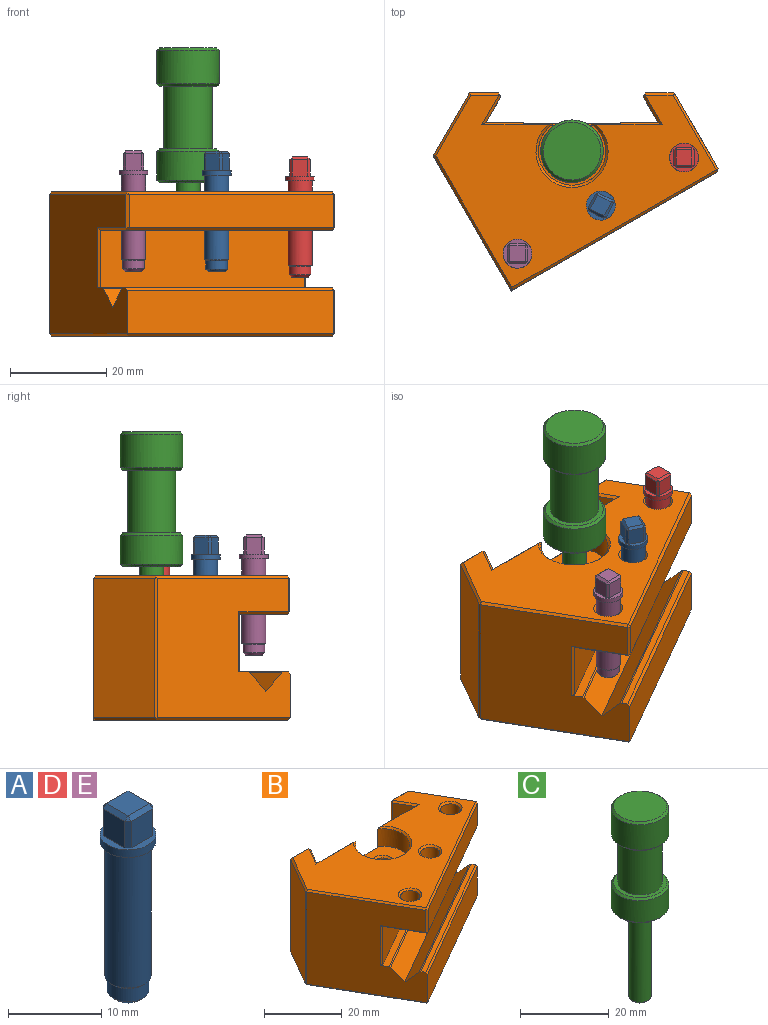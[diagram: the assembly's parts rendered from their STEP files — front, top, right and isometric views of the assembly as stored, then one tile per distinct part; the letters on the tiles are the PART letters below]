
ASSEMBLY  parts=5 mates=4
PART A: 25 faces, bbox 6x6x25 mm
  f0: cylinder r=3mm len=6mm, axis (0,0,-1), area 18.8mm2, adj f3,f5
  f1: cylinder r=2.25mm len=4.5mm, axis (0,0,-1), area 24.7mm2, adj f23,f24
  f2: plane 3.5x3.5mm, normal (0,0,-1), area 9.6mm2, adj f23
  f3: plane 6x6mm, normal (0,0,-1), area 8.6mm2, adj f0,f4
  f4: cylinder r=2.5mm len=17.5mm, axis (0,0,-1), area 274.9mm2, adj f3,f24
  f5: plane 6x6mm, normal (0,0,1), area 10.8mm2, adj f0,f6,f7,f8,f9,f11,f13,f16
  f6: plane 3.5x3.24mm, normal (0,1,0), area 11.3mm2, adj f5,f13,f19,f22
  f7: plane 3.5x3.24mm, normal (1,0,0), area 11.3mm2, adj f5,f11,f13,f14
  f8: plane 3.5x3.24mm, normal (0,-1,0), area 11.3mm2, adj f5,f11,f15,f16
  f9: plane 3.5x3.24mm, normal (-1,0,0), area 11.3mm2, adj f5,f16,f20,f22
  f10: plane 3.24x3.24mm, normal (0,0,1), area 10.5mm2, adj f14,f15,f19,f20
  f11: plane 3.5x0.5mm, normal (0.71,-0.71,0), area 2.5mm2, adj f5,f7,f8,f12
  f12: plane 0.5x0.5mm, normal (0.58,-0.58,0.58), area 0.2mm2, adj f11,f14,f15
  f13: plane 3.5x0.5mm, normal (0.71,0.71,0), area 2.5mm2, adj f5,f6,f7,f17
  f14: plane 3.24x0.5mm, normal (0.71,0,0.71), area 2.3mm2, adj f7,f10,f12,f17
  f15: plane 3.24x0.5mm, normal (0,-0.71,0.71), area 2.3mm2, adj f8,f10,f12,f18
  f16: plane 3.5x0.5mm, normal (-0.71,-0.71,0), area 2.5mm2, adj f5,f8,f9,f18
  f17: plane 0.5x0.5mm, normal (0.58,0.58,0.58), area 0.2mm2, adj f13,f14,f19
  f18: plane 0.5x0.5mm, normal (-0.58,-0.58,0.58), area 0.2mm2, adj f15,f16,f20
  f19: plane 3.24x0.5mm, normal (0,0.71,0.71), area 2.3mm2, adj f6,f10,f17,f21
  f20: plane 3.24x0.5mm, normal (-0.71,0,0.71), area 2.3mm2, adj f9,f10,f18,f21
  f21: plane 0.5x0.5mm, normal (-0.58,0.58,0.58), area 0.2mm2, adj f19,f20,f22
  f22: plane 3.5x0.5mm, normal (-0.71,0.71,0), area 2.5mm2, adj f5,f6,f9,f21
  f23: cone r=1.75mm half-angle=45deg, axis (0,0,1), area 8.9mm2, adj f1,f2
  f24: cone r=2mm half-angle=45deg, axis (0,0,1), area 5.3mm2, adj f1,f4
PART B: 89 faces, bbox 59.1x41.1x30 mm
  f0: plane 29x7.91mm, normal (0,1,0), area 229.4mm2, adj f2,f4,f14,f86
  f1: cylinder r=7mm len=14mm, axis (0,0,1), area 196.3mm2, adj f3,f5,f21,f88
  f2: plane 14.51x0.5mm, normal (0,0.71,0.71), area 8.2mm2, adj f0,f3,f19,f30,f86,f88
  f3: cone r=7mm half-angle=45deg, axis (0,0,1), area 25.4mm2, adj f1,f2,f19,f32,f88
  f4: plane 37.56x0.5mm, normal (0,0.71,-0.71), area 20.3mm2, adj f0,f11,f20,f33,f34,f86,f87,f88
  f5: plane 8.67x0.31mm, normal (0,0.71,0.71), area 3.5mm2, adj f1,f21,f88
  f6: plane 42.44x24.5mm, normal (0.5,-0.87,0), area 343mm2, adj f40,f41,f52,f53
  f7: plane 29x15.44mm, normal (0.87,0.5,0), area 343.4mm2, adj f53,f54,f61,f62,f64,f65,f68,f71
  f8: cylinder r=2.5mm len=7mm, axis (0,0,1), area 110mm2, adj f79,f80
  f9: cylinder r=2.5mm len=7mm, axis (0,0,1), area 110mm2, adj f81,f82
  f10: cylinder r=2.5mm len=7mm, axis (0,0,1), area 110mm2, adj f83,f84
  f11: plane 29x7.91mm, normal (0,1,0), area 229.4mm2, adj f4,f13,f32,f87
  f12: plane 29.5x5.81mm, normal (0,1,0), area 171.3mm2, adj f20,f43,f55,f62,f65
  f13: plane 29x5.4mm, normal (-0.87,-0.5,0), area 180.8mm2, adj f11,f33,f42,f43
  f14: plane 29x5.4mm, normal (0.87,-0.5,0), area 180.8mm2, adj f0,f30,f34,f35
  f15: plane 29x6.12mm, normal (0,1,0), area 177.3mm2, adj f16,f35,f36,f50
  f16: plane 29x12.8mm, normal (-0.87,0.5,0), area 428.6mm2, adj f15,f45,f56,f57
  f17: plane 29x27.83mm, normal (-0.87,-0.5,0), area 755.9mm2, adj f18,f25,f26,f27,f28,f37,f39,f40
  f18: plane 42.87x24.75mm, normal (0.5,-0.87,0), area 445.5mm2, adj f17,f66,f71,f72
  f19: plane 58.25x39.94mm, normal (0,0,1), area 1019.3mm2, adj f2,f3,f30,f32,f36,f41,f42,f45
  f20: plane 58.25x40.44mm, normal (0,0,-1), area 1269.7mm2, adj f4,f12,f33,f34,f43,f50,f56,f63
  f21: plane 14x12.5mm, normal (0,0,1), area 116.8mm2, adj f1,f5,f85
  f22: plane 5x5mm, normal (0,0,1), area 19.6mm2, adj f23
  f23: cylinder r=2.5mm len=9.5mm, axis (0,0,1), area 149.2mm2, adj f22,f85
  f24: plane 48.19x34.46mm, normal (0,0,-1), area 478.7mm2, adj f29,f39,f52,f61,f79,f82,f83
  f25: plane 43.51x25.87mm, normal (0,0,1), area 64mm2, adj f17,f72,f76,f78
  f26: plane 44.8x28.09mm, normal (-0.35,0.61,0.71), area 269.8mm2, adj f17,f27,f75,f78
  f27: plane 44.8x28.09mm, normal (0.35,-0.61,0.71), area 269.8mm2, adj f17,f26,f67,f73
  f28: plane 44.01x26.3mm, normal (0,0,1), area 88.9mm2, adj f17,f29,f37,f67,f68
  f29: plane 42.44x24.5mm, normal (0.5,-0.87,0), area 588mm2, adj f24,f28,f37,f64
  f30: plane 6.15x3.98mm, normal (0.61,-0.35,0.71), area 4.7mm2, adj f2,f14,f19,f31
  f31: plane 0.75x0.5mm, normal (0.77,0.45,0.45), area 0.2mm2, adj f30,f35,f36
  f32: plane 14.51x0.5mm, normal (0,0.71,0.71), area 8.2mm2, adj f3,f11,f19,f42,f87,f88
  f33: plane 6.4x3.98mm, normal (-0.61,-0.35,-0.71), area 4.8mm2, adj f4,f13,f20,f43
  f34: plane 6.15x3.98mm, normal (0.61,-0.35,-0.71), area 4.7mm2, adj f4,f14,f20,f44
  f35: plane 29x0.75mm, normal (0.87,0.5,0), area 25.1mm2, adj f14,f15,f31,f44
  f36: plane 6.12x0.5mm, normal (0,0.71,0.71), area 4.2mm2, adj f15,f19,f31,f45
  f37: plane 12.5x0.68mm, normal (-0.26,-0.97,0), area 8.7mm2, adj f17,f28,f29,f39
  f38: plane 0.68x0.5mm, normal (-0.21,-0.79,0.58), area 0.2mm2, adj f40,f41,f46
  f39: plane 10.39x6.43mm, normal (-0.61,-0.35,-0.71), area 8.3mm2, adj f17,f24,f37,f47
  f40: plane 7x0.68mm, normal (-0.26,-0.97,0), area 4.9mm2, adj f6,f17,f38,f47
  f41: plane 42.69x24.93mm, normal (0.35,-0.61,0.71), area 34.6mm2, adj f6,f19,f38,f48
  f42: plane 6.15x3.98mm, normal (-0.61,-0.35,0.71), area 4.7mm2, adj f13,f19,f32,f49
  f43: plane 29.5x0.75mm, normal (-0.87,0.5,0), area 25.4mm2, adj f12,f13,f20,f33,f49
  f44: plane 0.75x0.5mm, normal (0.77,0.45,-0.45), area 0.2mm2, adj f34,f35,f50
  f45: plane 13.05x7.68mm, normal (-0.61,0.35,0.71), area 10.3mm2, adj f16,f19,f36,f51
  f46: plane 27.64x16.25mm, normal (-0.61,-0.35,0.71), area 22.4mm2, adj f17,f19,f38,f51
  f47: plane 0.68x0.5mm, normal (-0.21,-0.79,-0.58), area 0.2mm2, adj f39,f40,f52
  f48: plane 0.68x0.5mm, normal (0.79,-0.21,0.58), area 0.2mm2, adj f41,f53,f54
  f49: plane 0.75x0.5mm, normal (-0.77,0.45,0.45), area 0.2mm2, adj f42,f43,f55
  f50: plane 6.12x0.5mm, normal (0,0.71,-0.71), area 4.2mm2, adj f15,f20,f44,f56
  f51: plane 0.5x0.5mm, normal (-0.76,0,0.65), area 0.2mm2, adj f45,f46,f57
  f52: plane 42.69x24.93mm, normal (0.35,-0.61,-0.71), area 34.6mm2, adj f6,f24,f47,f58
  f53: plane 7x0.68mm, normal (0.97,-0.26,0), area 4.9mm2, adj f6,f7,f48,f58
  f54: plane 15.69x9.35mm, normal (0.61,0.35,0.71), area 12.6mm2, adj f7,f19,f48,f59
  f55: plane 5.81x0.5mm, normal (0,0.71,0.71), area 4.1mm2, adj f12,f19,f49,f59
  f56: plane 13.05x7.68mm, normal (-0.61,0.35,-0.71), area 10.3mm2, adj f16,f20,f50,f60
  f57: plane 29x0.5mm, normal (-1,0,0), area 14.5mm2, adj f16,f17,f51,f60
  f58: plane 0.68x0.5mm, normal (0.79,-0.21,-0.58), area 0.2mm2, adj f52,f53,f61
  f59: plane 0.5x0.5mm, normal (0.38,0.65,0.65), area 0.2mm2, adj f54,f55,f62
  f60: plane 0.5x0.5mm, normal (-0.76,0,-0.65), area 0.2mm2, adj f56,f57,f63
  f61: plane 10.64x6.18mm, normal (0.61,0.35,-0.71), area 8.3mm2, adj f7,f24,f58,f64
  f62: plane 29.25x0.43mm, normal (0.5,0.87,0), area 14.6mm2, adj f7,f12,f59,f65
  f63: plane 28.08x16.25mm, normal (-0.61,-0.35,-0.71), area 22.5mm2, adj f17,f20,f60,f66
  f64: plane 13x0.68mm, normal (0.97,-0.26,0), area 8.8mm2, adj f7,f29,f61,f68
  f65: plane 15.94x9.64mm, normal (0.61,0.35,-0.71), area 12.9mm2, adj f7,f12,f20,f62,f69
  f66: plane 42.87x25.18mm, normal (0.35,-0.61,-0.71), area 34.8mm2, adj f18,f20,f63,f69
  f67: plane 43.05x25.06mm, normal (0.19,-0.33,0.92), area 18.9mm2, adj f17,f27,f28,f70
  f68: plane 2.24x1.33mm, normal (0.61,0.35,0.71), area 1.4mm2, adj f7,f28,f64,f70
  f69: plane 0.68x0.5mm, normal (0.79,-0.21,-0.58), area 0.2mm2, adj f65,f66,f71
  f70: plane 0.56x0.5mm, normal (0.73,0.1,0.68), area 0.1mm2, adj f67,f68,f73
  f71: plane 9x0.68mm, normal (0.97,-0.26,0), area 6.4mm2, adj f7,f18,f69,f74
  f72: plane 43.12x25.18mm, normal (0.35,-0.61,0.71), area 35mm2, adj f17,f18,f25,f74
  f73: plane 4.56x3.89mm, normal (0.86,-0.08,0.5), area 4mm2, adj f7,f27,f70,f75
  f74: plane 0.68x0.5mm, normal (0.79,-0.21,0.58), area 0.2mm2, adj f71,f72,f76
  f75: plane 4.56x3.64mm, normal (0.36,0.79,0.5), area 4mm2, adj f7,f26,f73,f77
  f76: plane 1.37x1.08mm, normal (0.61,0.35,0.71), area 0.9mm2, adj f7,f25,f74,f77
  f77: plane 0.61x0.5mm, normal (0.45,0.58,0.68), area 0.1mm2, adj f75,f76,f78
  f78: plane 43.05x25.06mm, normal (-0.19,0.33,0.92), area 18.9mm2, adj f17,f25,f26,f77
  f79: cone r=3mm half-angle=45deg, axis (0,0,-1), area 12.2mm2, adj f8,f24
  f80: cone r=2.5mm half-angle=45deg, axis (0,0,1), area 12.2mm2, adj f8,f19
  f81: cone r=2.5mm half-angle=45deg, axis (0,0,1), area 12.2mm2, adj f9,f19
  f82: cone r=3mm half-angle=45deg, axis (0,0,-1), area 12.2mm2, adj f9,f24
  f83: cone r=3mm half-angle=45deg, axis (0,0,-1), area 12.2mm2, adj f10,f24
  f84: cone r=2.5mm half-angle=45deg, axis (0,0,1), area 12.2mm2, adj f10,f19
  f85: cone r=2.5mm half-angle=45deg, axis (0,0,1), area 12.2mm2, adj f21,f23
  f86: plane 29.4x0.2mm, normal (1,0,0), area 5.8mm2, adj f0,f2,f4,f88
  f87: plane 29.4x0.2mm, normal (-1,0,0), area 5.8mm2, adj f4,f11,f32,f88
  f88: plane 29.41x20.01mm, normal (0,1,0), area 540.9mm2, adj f1,f2,f3,f4,f5,f32,f86,f87
PART C: 14 faces, bbox 13x13x53 mm
  f0: plane 12x12mm, normal (0,0,1), area 113.1mm2, adj f13
  f1: cylinder r=6.5mm len=13mm, axis (0,0,1), area 285.9mm2, adj f12,f13
  f2: plane 12x12mm, normal (0,0,-1), area 34.6mm2, adj f3,f12
  f3: cylinder r=5mm len=13mm, axis (0,0,1), area 408.4mm2, adj f2,f4
  f4: plane 12x12mm, normal (0,0,1), area 34.6mm2, adj f3,f11
  f5: cylinder r=6.5mm len=13mm, axis (0,0,1), area 245mm2, adj f10,f11
  f6: plane 12x12mm, normal (0,0,-1), area 93.5mm2, adj f7,f10
  f7: cylinder r=2.5mm len=24.5mm, axis (0,0,1), area 384.8mm2, adj f6,f9
  f8: plane 4x4mm, normal (0,0,-1), area 12.6mm2, adj f9
  f9: cone r=2.5mm half-angle=45deg, axis (0,0,1), area 10mm2, adj f7,f8
  f10: cone r=6.5mm half-angle=45deg, axis (0,0,1), area 27.8mm2, adj f5,f6
  f11: cone r=6mm half-angle=45deg, axis (0,0,-1), area 27.8mm2, adj f4,f5
  f12: cone r=6.5mm half-angle=45deg, axis (0,0,1), area 27.8mm2, adj f1,f2
  f13: cone r=6mm half-angle=45deg, axis (0,0,-1), area 27.8mm2, adj f0,f1
PART D: same geometry as A
PART E: same geometry as A
PLACE A rot(axis=(0,0,1),153.2deg) t=(18.47,17.01,16.98)mm
PLACE B t=(-12.53,10.56,0)mm
PLACE C rot(axis=(0,0,-1),165.8deg) t=(12.48,28.29,31.92)mm
PLACE D t=(35.79,27.01,15.83)mm
PLACE E t=(1.15,7.01,17.08)mm
MATE cylindrical A.f0 <-> B.f9  axis (0,0,-1) through (18.47,17.01,24.65)mm
MATE cylindrical C.f1 <-> B.f1  axis (0,0,1) through (12.48,28.29,19.67)mm
MATE cylindrical D.f0 <-> B.f10  axis (0,0,-1) through (35.79,27.01,23.5)mm
MATE cylindrical E.f0 <-> B.f8  axis (0,0,-1) through (1.15,7.01,16)mm
